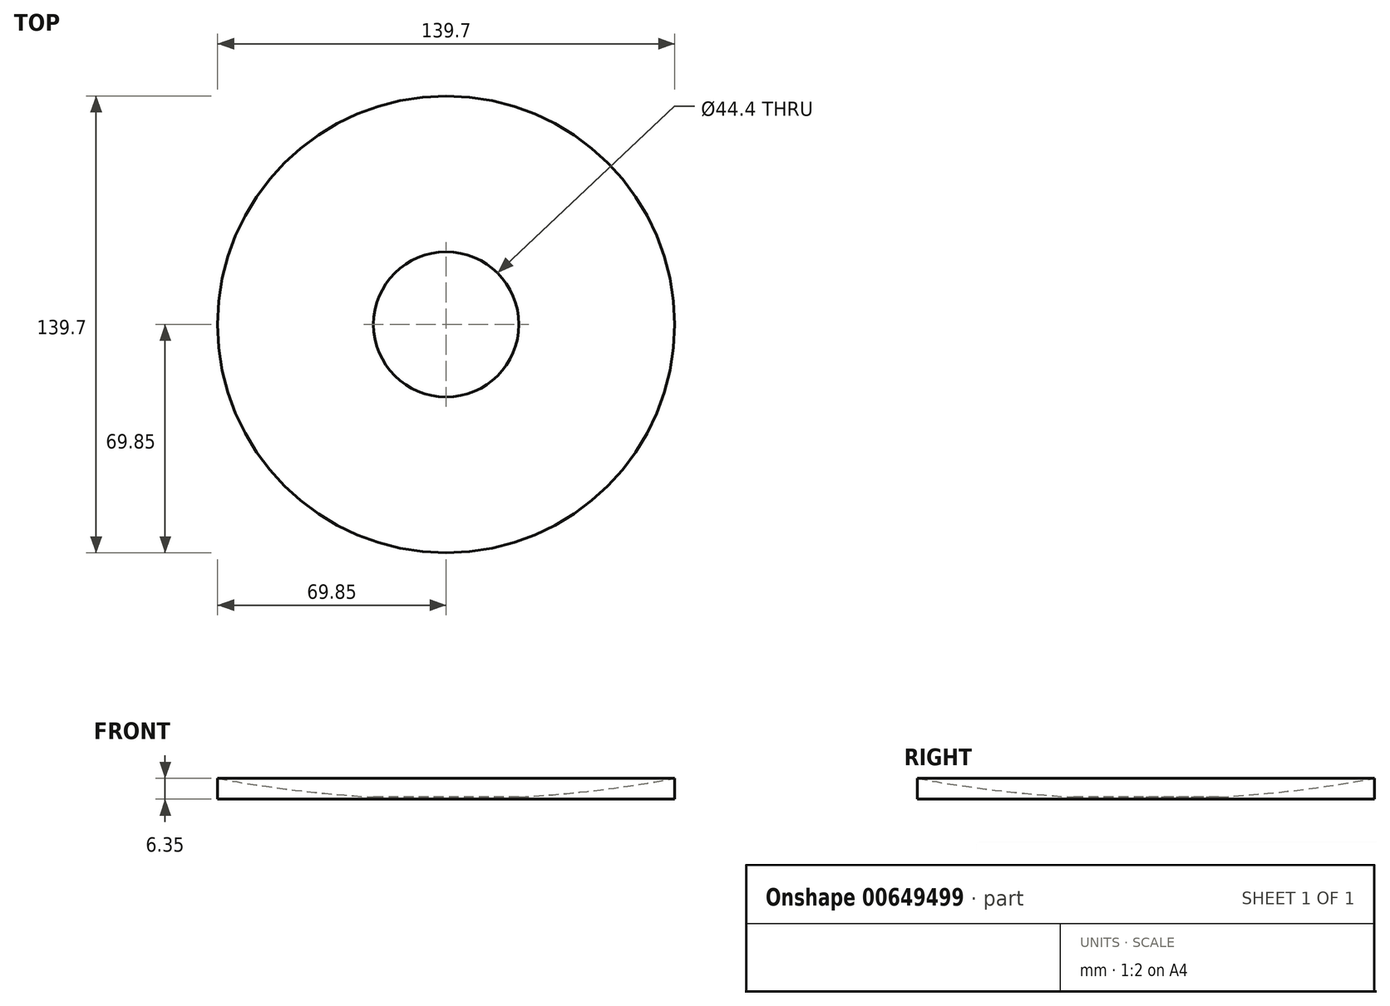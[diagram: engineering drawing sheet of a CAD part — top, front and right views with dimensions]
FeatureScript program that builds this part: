
annotation { "Feature Type Name" : "Feature", "Feature Type Description" : "" }
export const myFeature = defineFeature(function(context is Context, id is Id, definition is map)
    precondition{}
    {
        {
            var Q0;
            Q0=qCreatedBy(makeId("Front.planeOp"),FACE);
            var sketch = newSketch(context, id + "F0", { "sketchPlane" : qUnion([Q0])});
            skLineSegment(sketch, "E0", {"start": v(22.2, 0) * mm, "end": v(69.85, 0) * mm});
            skLineSegment(sketch, "E1", {"start": v(69.85, 0) * mm, "end": v(69.85, 6.35) * mm});
            skArc(sketch, "E2", {"start": v(22.2, 0.64) * mm, "mid": v(46.11, 2.75) * mm, "end": v(69.85, 6.35) * mm});
            skLineSegment(sketch, "E3", {"start": v(22.2, 0.64) * mm, "end": v(22.2, 0) * mm});
            skLineSegment(sketch, "E4", {"start": v(0, 20.76) * mm, "end": v(0, -7.87) * mm, "construction": true});
            skSolve(sketch);
        }
        {
            var Q0;
            Q0 = qSketchRegion(id + "F0", true);
            var Q1;
            Q1=sQuery(id+"F0.wireOp",EDGE,"E4");
            revolve(context, id + "F1", {"entities" : qUnion([Q0]), "axis" : qUnion([Q1]), "revolveType" : RevolveType.FULL});
        }
    });
